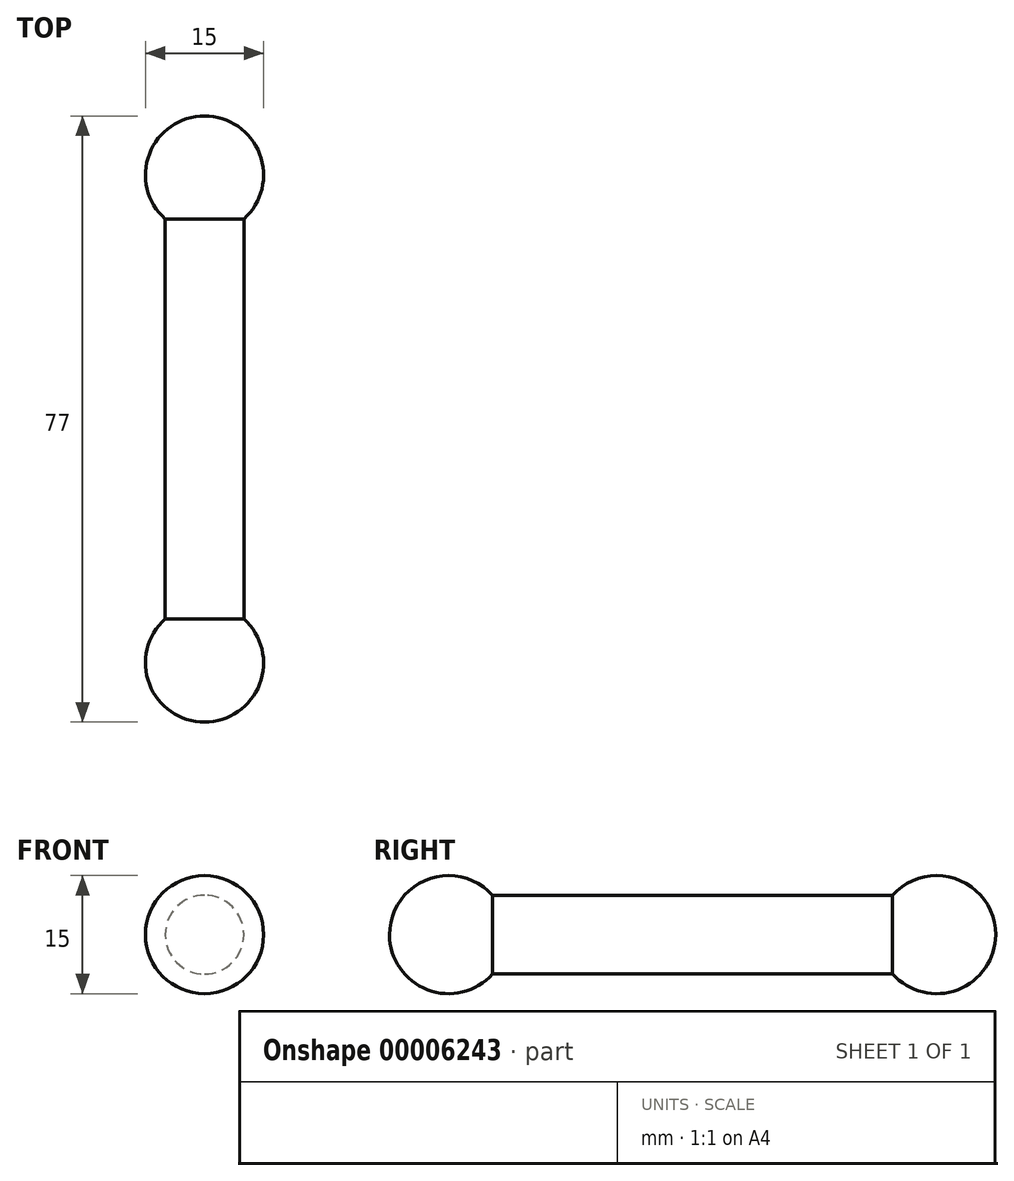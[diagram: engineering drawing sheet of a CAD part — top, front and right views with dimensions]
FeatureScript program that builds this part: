
annotation { "Feature Type Name" : "Feature", "Feature Type Description" : "" }
export const myFeature = defineFeature(function(context is Context, id is Id, definition is map)
    precondition{}
    {
        {
            var Q0;
            Q0=qCreatedBy(makeId("Right.planeOp"),FACE);
            var sketch = newSketch(context, id + "F0", { "sketchPlane" : qUnion([Q0])});
            skArc(sketch, "E0", {"start": v(5.6, 5) * mm, "mid": v(-2.68, 7) * mm, "end": v(-7.5, 0) * mm});
            skArc(sketch, "E1", {"start": v(69.5, 0) * mm, "mid": v(64.68, 7) * mm, "end": v(56.4, 5) * mm});
            skLineSegment(sketch, "E2.rect.bottom", {"start": v(56.4, 5) * mm, "end": v(5.6, 5) * mm});
            skPoint(sketch, "E2.rect.right.end.orphan", {"position": v(-53.54, -5) * mm});
            skPoint(sketch, "E3.orphan", {"position": v(-53.54, 5) * mm});
            skPoint(sketch, "E2.rect.left.end.orphan", {"position": v(53.54, -5) * mm});
            skLineSegment(sketch, "E4", {"start": v(-7.5, 0) * mm, "end": v(69.5, 0) * mm});
            skPoint(sketch, "E5.orphan", {"position": v(53.54, 5) * mm});
            skSolve(sketch);
        }
        {
            var Q0;
            Q0=makeQuery(id+"F0.imprint","IMPRINT",FACE,{"disambiguationData":[TD([[makeQuery(id+"F0.imprint","IMPRINT",EDGE,{"derivedFrom":sQuery(id+"F0.wireOp",EDGE,"E0")}),1.0]])]});
            var Q1;
            Q1=sQuery(id+"F0.wireOp",EDGE,"E4");
            revolve(context, id + "F1", {"entities" : qUnion([Q0]), "axis" : qUnion([Q1]), "revolveType" : RevolveType.FULL});
        }
    });
